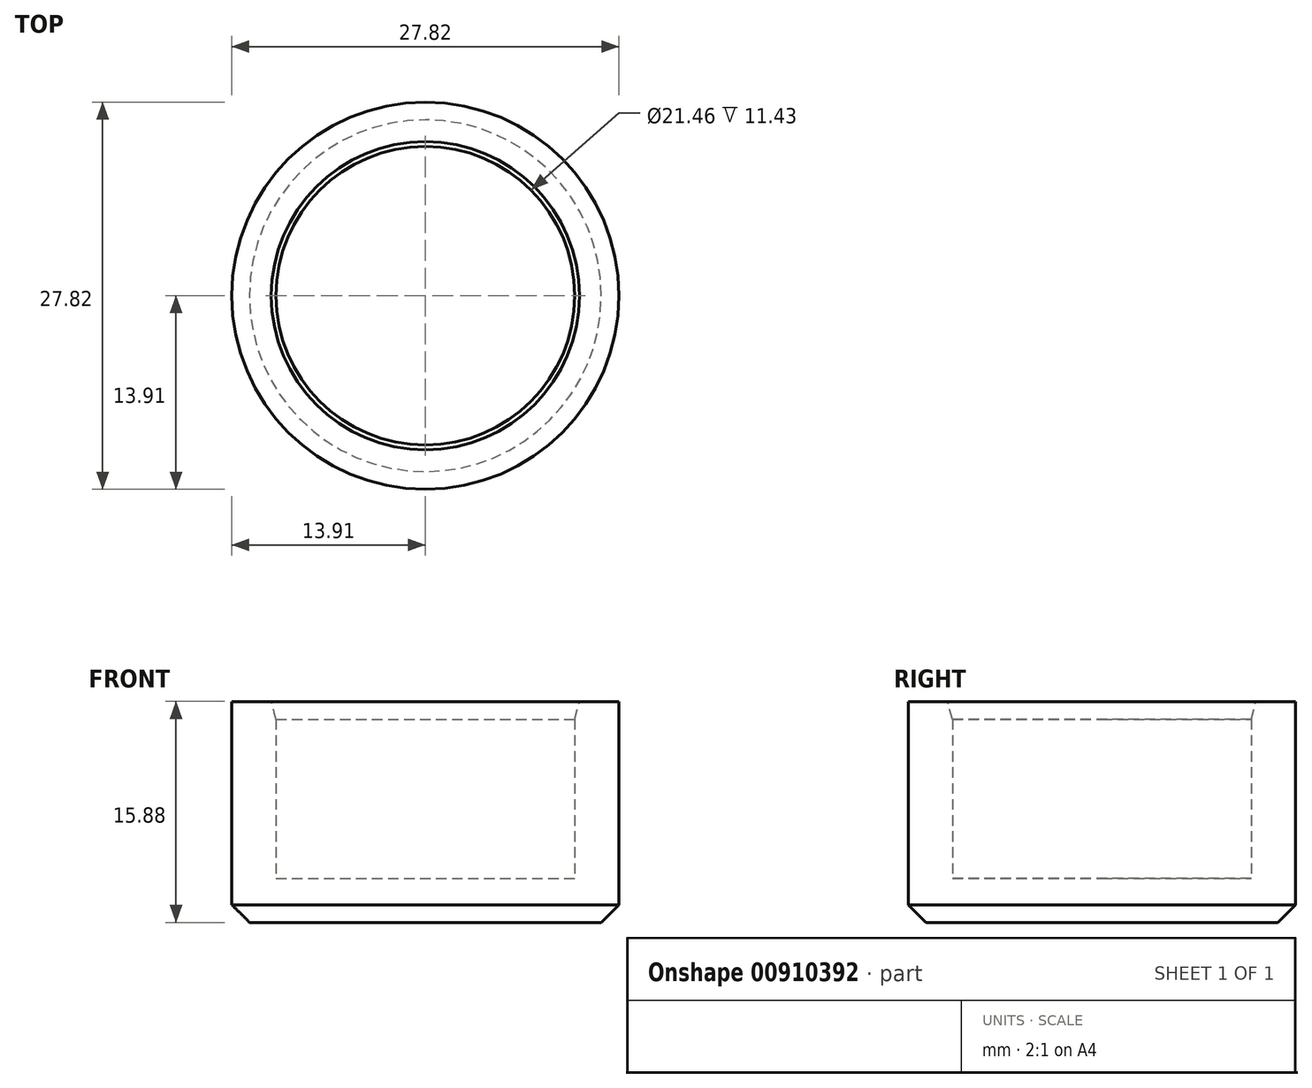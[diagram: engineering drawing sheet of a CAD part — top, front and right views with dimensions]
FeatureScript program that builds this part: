
annotation { "Feature Type Name" : "Feature", "Feature Type Description" : "" }
export const myFeature = defineFeature(function(context is Context, id is Id, definition is map)
    precondition{}
    {
        {
            var Q0;
            Q0=qCreatedBy(makeId("Front.planeOp"),FACE);
            var sketch = newSketch(context, id + "F0", { "sketchPlane" : qUnion([Q0])});
            skLineSegment(sketch, "E0", {"start": v(0, 0) * mm, "end": v(12.64, 0) * mm});
            skLineSegment(sketch, "E1", {"start": v(13.9, 1.27) * mm, "end": v(13.9, 15.88) * mm});
            skLineSegment(sketch, "E2", {"start": v(13.9, 15.88) * mm, "end": v(11.07, 15.88) * mm});
            skLineSegment(sketch, "E3", {"start": v(10.73, 14.6) * mm, "end": v(10.73, 3.18) * mm});
            skLineSegment(sketch, "E4", {"start": v(10.73, 3.18) * mm, "end": v(0, 3.17) * mm});
            skLineSegment(sketch, "E5", {"start": v(0, 3.17) * mm, "end": v(0, 0) * mm});
            skLineSegment(sketch, "E6", {"start": v(10.73, 14.6) * mm, "end": v(11.07, 15.88) * mm});
            skLineSegment(sketch, "E7", {"start": v(0, 3.17) * mm, "end": v(0, 13.73) * mm, "construction": true});
            skLineSegment(sketch, "E8", {"start": v(12.64, 0) * mm, "end": v(13.9, 1.27) * mm});
            skSolve(sketch);
        }
        {
            var Q0;
            Q0 = qSketchRegion(id + "F0", true);
            var Q1;
            Q1=sQuery(id+"F0.wireOp",EDGE,"E7");
            revolve(context, id + "F1", {"surfaceOperationType" : NewSurfaceOperationType.NEW, "entities" : qUnion([Q0]), "axis" : qUnion([Q1]), "revolveType" : RevolveType.FULL});
        }
    });
